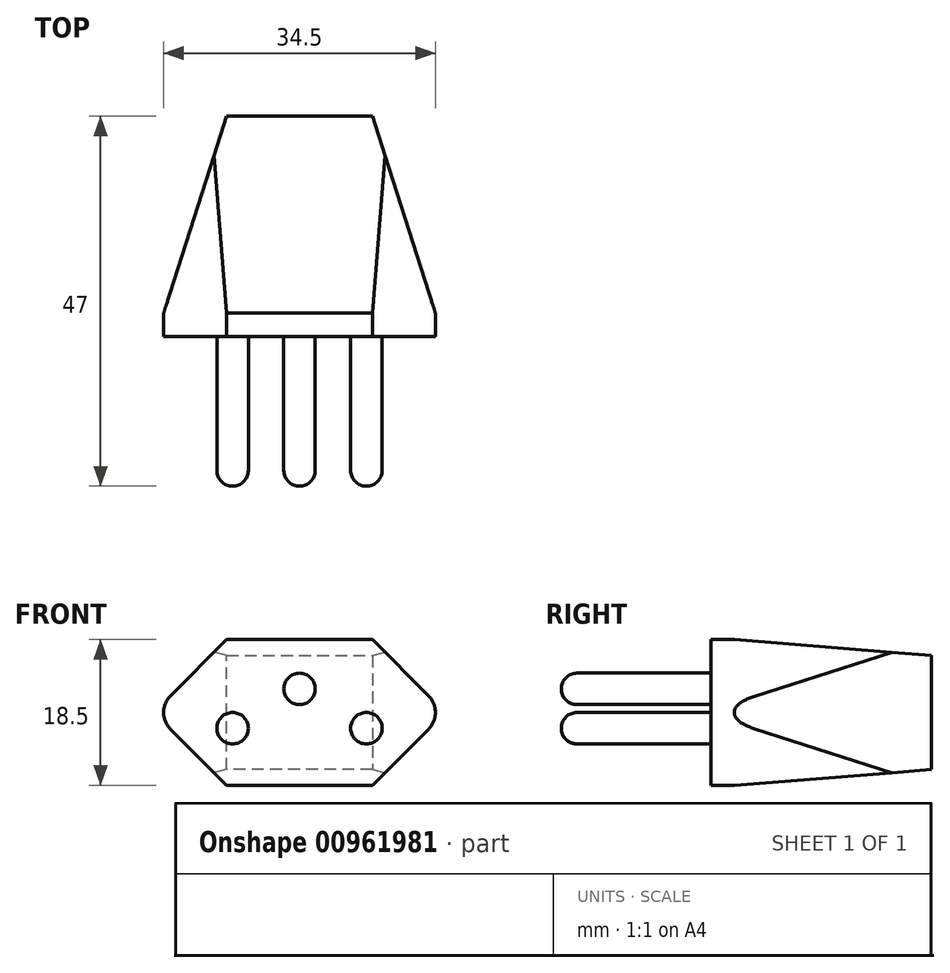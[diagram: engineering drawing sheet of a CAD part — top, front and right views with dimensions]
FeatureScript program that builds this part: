
annotation { "Feature Type Name" : "Feature", "Feature Type Description" : "" }
export const myFeature = defineFeature(function(context is Context, id is Id, definition is map)
    precondition{}
    {
        {
            var Q0;
            Q0=qCreatedBy(makeId("Front.planeOp"),FACE);
            var sketch = newSketch(context, id + "F0", { "sketchPlane" : qUnion([Q0])});
            skLineSegment(sketch, "E0.bottom", {"start": v(17.25, -9.25) * mm, "end": v(-17.25, -9.25) * mm});
            skLineSegment(sketch, "E0.top", {"start": v(17.25, 9.25) * mm, "end": v(-17.25, 9.25) * mm});
            skLineSegment(sketch, "E0.left", {"start": v(17.25, -9.25) * mm, "end": v(17.25, 9.25) * mm});
            skLineSegment(sketch, "E0.right", {"start": v(-17.25, -9.25) * mm, "end": v(-17.25, 9.25) * mm});
            skPoint(sketch, "E0.middle", {"position": v(0, 0) * mm});
            skSolve(sketch);
        }
        {
            var Q0;
            Q0 = qSketchRegion(id + "F0", true);
            extrude(context, id + "F1", {"entities" : qUnion([Q0]), "oppositeDirection" : true, "depth" : 28 * mm, "offsetDistance" : 25 * mm});
        }
        {
            var Q0;
            Q0=makeQuery(id+"F1.opExtrude","CAP_FACE",FACE,{"disambiguationData":[OSD([sQuery(id+"F0.wireOp",EDGE,"E0.bottom"),sQuery(id+"F0.wireOp",EDGE,"E0.top"),sQuery(id+"F0.wireOp",EDGE,"E0.left"),sQuery(id+"F0.wireOp",EDGE,"E0.right")])],"isStart":true});
            var sketch = newSketch(context, id + "F2", { "sketchPlane" : qUnion([Q0])});
            skCircle(sketch, "E1", {"center": v(-8.5, -2) * mm, "radius": 2 * mm});
            skPoint(sketch, "E2", {"position": v(0, 0) * mm});
            skCircle(sketch, "E3", {"center": v(8.5, -2) * mm, "radius": 2 * mm});
            skCircle(sketch, "E4", {"center": v(0, 3) * mm, "radius": 2 * mm});
            skLineSegment(sketch, "E5", {"start": v(-8.5, -2) * mm, "end": v(8.5, -2) * mm, "construction": true});
            skSolve(sketch);
        }
        {
            var Q0;
            Q0 = qSketchRegion(id + "F2", true);
            extrude(context, id + "F3", {"entities" : qUnion([Q0]), "operationType" : NewBodyOperationType.ADD, "depth" : 19 * mm, "offsetDistance" : 25 * mm});
        }
        {
            var Q0;
            Q0=makeQuery(id+"F1.opExtrude","SWEPT_EDGE",EDGE,{"disambiguationData":[OSD([sQuery(id+"F0.wireOp",EDGE,"E0.top"),sQuery(id+"F0.wireOp",EDGE,"E0.left")])]});
            var Q1;
            Q1=makeQuery(id+"F1.opExtrude","SWEPT_EDGE",EDGE,{"disambiguationData":[OSD([sQuery(id+"F0.wireOp",EDGE,"E0.top"),sQuery(id+"F0.wireOp",EDGE,"E0.right")])]});
            var Q2;
            Q2=makeQuery(id+"F1.opExtrude","SWEPT_EDGE",EDGE,{"disambiguationData":[OSD([sQuery(id+"F0.wireOp",EDGE,"E0.bottom"),sQuery(id+"F0.wireOp",EDGE,"E0.left")])]});
            var Q3;
            Q3=makeQuery(id+"F1.opExtrude","SWEPT_EDGE",EDGE,{"disambiguationData":[OSD([sQuery(id+"F0.wireOp",EDGE,"E0.bottom"),sQuery(id+"F0.wireOp",EDGE,"E0.right")])]});
            var Q4;
            Q4=makeQuery(id+"F6.opChamfer","BLEND_EDGE",EDGE,{"blendedFrom":[makeQuery(id+"F1.opExtrude","CAP_EDGE",EDGE,{"disambiguationData":[OSD([sQuery(id+"F0.wireOp",EDGE,"E0.top")])],"isStart":false}),makeQuery(id+"F5.opChamfer","BLEND_FACE",FACE,{"disambiguationData":[OSD([sQuery(id+"F0.wireOp",EDGE,"E0.right")])]})],"blendedInto":[makeQuery(id+"F5.opChamfer","BLEND_FACE",FACE,{"disambiguationData":[OSD([sQuery(id+"F0.wireOp",EDGE,"E0.right")])]})]});
            var Q5;
            Q5=makeQuery(id+"F6.opChamfer","BLEND_EDGE",EDGE,{"blendedFrom":[makeQuery(id+"F1.opExtrude","CAP_EDGE",EDGE,{"disambiguationData":[OSD([sQuery(id+"F0.wireOp",EDGE,"E0.top")])],"isStart":false}),makeQuery(id+"F5.opChamfer","BLEND_FACE",FACE,{"disambiguationData":[OSD([sQuery(id+"F0.wireOp",EDGE,"E0.left")])]})],"blendedInto":[makeQuery(id+"F5.opChamfer","BLEND_FACE",FACE,{"disambiguationData":[OSD([sQuery(id+"F0.wireOp",EDGE,"E0.left")])]})]});
            var Q6;
            Q6=makeQuery(id+"F6.opChamfer","BLEND_EDGE",EDGE,{"blendedFrom":[makeQuery(id+"F1.opExtrude","CAP_EDGE",EDGE,{"disambiguationData":[OSD([sQuery(id+"F0.wireOp",EDGE,"E0.bottom")])],"isStart":false}),makeQuery(id+"F5.opChamfer","BLEND_FACE",FACE,{"disambiguationData":[OSD([sQuery(id+"F0.wireOp",EDGE,"E0.left")])]})],"blendedInto":[makeQuery(id+"F5.opChamfer","BLEND_FACE",FACE,{"disambiguationData":[OSD([sQuery(id+"F0.wireOp",EDGE,"E0.left")])]})]});
            var Q7;
            Q7=makeQuery(id+"F6.opChamfer","BLEND_EDGE",EDGE,{"blendedFrom":[makeQuery(id+"F1.opExtrude","CAP_EDGE",EDGE,{"disambiguationData":[OSD([sQuery(id+"F0.wireOp",EDGE,"E0.bottom")])],"isStart":false}),makeQuery(id+"F5.opChamfer","BLEND_FACE",FACE,{"disambiguationData":[OSD([sQuery(id+"F0.wireOp",EDGE,"E0.right")])]})],"blendedInto":[makeQuery(id+"F5.opChamfer","BLEND_FACE",FACE,{"disambiguationData":[OSD([sQuery(id+"F0.wireOp",EDGE,"E0.right")])]})]});
            chamfer(context, id + "F4", {"entities" : qUnion([Q0, Q1, Q2, Q3, Q4, Q5, Q6, Q7]), "width" : 8 * mm, "tangentPropagation" : true});
        }
        {
            var Q0;
            Q0=makeQuery(id+"F1.opExtrude","CAP_EDGE",EDGE,{"disambiguationData":[OSD([sQuery(id+"F0.wireOp",EDGE,"E0.left")])],"isStart":false});
            var Q1;
            Q1=makeQuery(id+"F1.opExtrude","CAP_EDGE",EDGE,{"disambiguationData":[OSD([sQuery(id+"F0.wireOp",EDGE,"E0.right")])],"isStart":false});
            chamfer(context, id + "F5", {"entities" : qUnion([Q0, Q1]), "chamferType" : ChamferType.TWO_OFFSETS, "width1" : 25 * mm, "oppositeDirection" : false, "width2" : 8 * mm, "tangentPropagation" : true});
        }
        {
            var Q0;
            Q0=makeQuery(id+"F1.opExtrude","CAP_EDGE",EDGE,{"disambiguationData":[OSD([sQuery(id+"F0.wireOp",EDGE,"E0.top")])],"isStart":false});
            var Q1;
            Q1=makeQuery(id+"F1.opExtrude","CAP_EDGE",EDGE,{"disambiguationData":[OSD([sQuery(id+"F0.wireOp",EDGE,"E0.bottom")])],"isStart":false});
            chamfer(context, id + "F6", {"entities" : qUnion([Q0, Q1]), "chamferType" : ChamferType.TWO_OFFSETS, "width1" : 25 * mm, "oppositeDirection" : false, "width2" : 2 * mm, "tangentPropagation" : true});
        }
        {
            var Q0;
            Q0=makeQuery(id+"F3.opExtrude","CAP_FACE",FACE,{"disambiguationData":[OSD([sQuery(id+"F2.wireOp",EDGE,"E1")])],"isStart":false});
            var Q1;
            Q1=makeQuery(id+"F3.opExtrude","CAP_EDGE",EDGE,{"disambiguationData":[OSD([sQuery(id+"F2.wireOp",EDGE,"E3")])],"isStart":false});
            var Q2;
            Q2=makeQuery(id+"F3.opExtrude","CAP_EDGE",EDGE,{"disambiguationData":[OSD([sQuery(id+"F2.wireOp",EDGE,"E4")])],"isStart":false});
            fillet(context, id + "F7", {"entities" : qUnion([Q0, Q1, Q2]), "radius" : 2 * mm, "tangentPropagation" : true, "allowEdgeOverflow" : false});
        }
        {
            var Q0;
            {var subQ0=sQuery(id+"F0.wireOp",EDGE,"E0.right");Q0=makeQuery(id+"F4.opChamfer","BLEND_EDGE",EDGE,{"blendedFrom":[makeQuery(id+"F1.opExtrude","SWEPT_EDGE",EDGE,{"disambiguationData":[OSD([sQuery(id+"F0.wireOp",EDGE,"E0.top"),subQ0])]}),makeQuery(id+"F1.opExtrude","SWEPT_FACE",FACE,{"disambiguationData":[OSD([subQ0])]})],"blendedInto":[makeQuery(id+"F1.opExtrude","SWEPT_FACE",FACE,{"disambiguationData":[OSD([subQ0])]})]});}
            var Q1;
            {var subQ0=sQuery(id+"F0.wireOp",EDGE,"E0.right");Q1=makeQuery(id+"F4.opChamfer","BLEND_EDGE",EDGE,{"blendedFrom":[makeQuery(id+"F1.opExtrude","SWEPT_EDGE",EDGE,{"disambiguationData":[OSD([sQuery(id+"F0.wireOp",EDGE,"E0.bottom"),subQ0])]}),makeQuery(id+"F1.opExtrude","SWEPT_FACE",FACE,{"disambiguationData":[OSD([subQ0])]})],"blendedInto":[makeQuery(id+"F1.opExtrude","SWEPT_FACE",FACE,{"disambiguationData":[OSD([subQ0])]})]});}
            var Q2;
            {var subQ0=sQuery(id+"F0.wireOp",EDGE,"E0.left");Q2=makeQuery(id+"F4.opChamfer","BLEND_EDGE",EDGE,{"blendedFrom":[makeQuery(id+"F1.opExtrude","SWEPT_EDGE",EDGE,{"disambiguationData":[OSD([sQuery(id+"F0.wireOp",EDGE,"E0.top"),subQ0])]}),makeQuery(id+"F1.opExtrude","SWEPT_FACE",FACE,{"disambiguationData":[OSD([subQ0])]})],"blendedInto":[makeQuery(id+"F1.opExtrude","SWEPT_FACE",FACE,{"disambiguationData":[OSD([subQ0])]})]});}
            var Q3;
            {var subQ0=sQuery(id+"F0.wireOp",EDGE,"E0.left");Q3=makeQuery(id+"F4.opChamfer","BLEND_EDGE",EDGE,{"blendedFrom":[makeQuery(id+"F1.opExtrude","SWEPT_EDGE",EDGE,{"disambiguationData":[OSD([sQuery(id+"F0.wireOp",EDGE,"E0.bottom"),subQ0])]}),makeQuery(id+"F1.opExtrude","SWEPT_FACE",FACE,{"disambiguationData":[OSD([subQ0])]})],"blendedInto":[makeQuery(id+"F1.opExtrude","SWEPT_FACE",FACE,{"disambiguationData":[OSD([subQ0])]})]});}
            fillet(context, id + "F8", {"entities" : qUnion([Q0, Q1, Q2, Q3]), "radius" : 2.8 * mm, "tangentPropagation" : true, "allowEdgeOverflow" : false});
        }
    });
